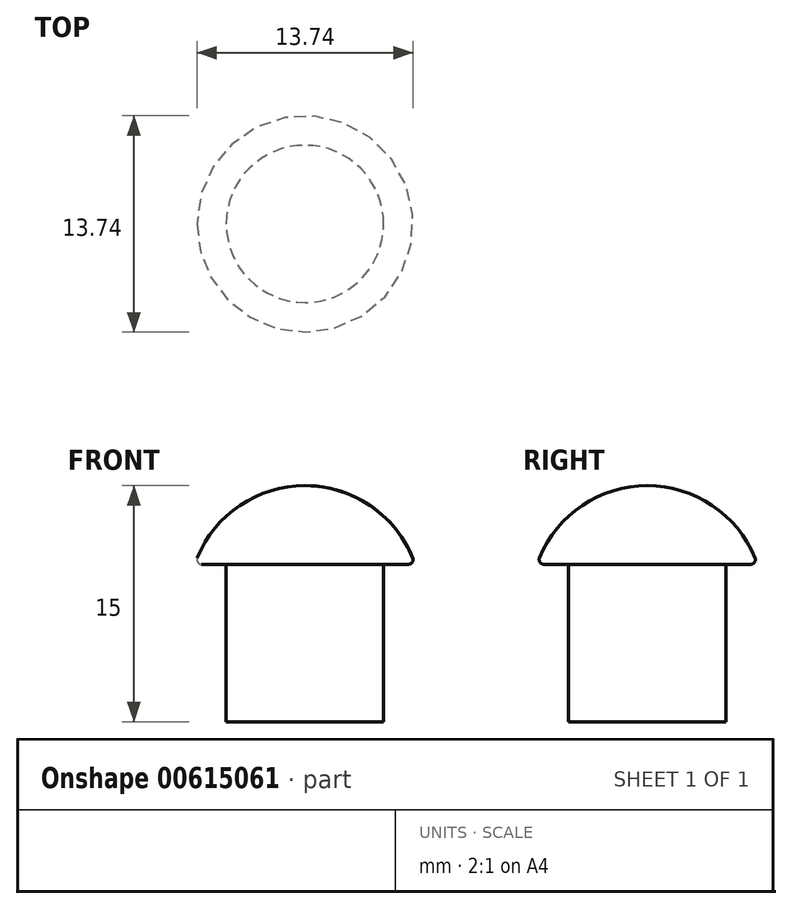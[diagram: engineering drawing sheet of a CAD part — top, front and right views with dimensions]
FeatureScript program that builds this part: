
annotation { "Feature Type Name" : "Feature", "Feature Type Description" : "" }
export const myFeature = defineFeature(function(context is Context, id is Id, definition is map)
    precondition{}
    {
        {
            var Q0;
            Q0=qCreatedBy(makeId("Front.planeOp"),FACE);
            var sketch = newSketch(context, id + "F0", { "sketchPlane" : qUnion([Q0])});
            skLineSegment(sketch, "E0", {"start": v(0, 0) * mm, "end": v(5, 0) * mm});
            skLineSegment(sketch, "E1", {"start": v(5, 0) * mm, "end": v(5, 10) * mm});
            skLineSegment(sketch, "E2", {"start": v(5, 10) * mm, "end": v(7, 10) * mm});
            skArc(sketch, "E3", {"start": v(7, 10) * mm, "mid": v(4.3, 13.62) * mm, "end": v(0, 15) * mm});
            skLineSegment(sketch, "E4", {"start": v(0, 0) * mm, "end": v(0, 19.87) * mm, "construction": true});
            skLineSegment(sketch, "E5", {"start": v(0, 0) * mm, "end": v(0, 15) * mm});
            skSolve(sketch);
        }
        {
            var Q0;
            Q0 = qSketchRegion(id + "F0", true);
            var Q1;
            Q1=sQuery(id+"F0.wireOp",EDGE,"E4");
            revolve(context, id + "F1", {"entities" : qUnion([Q0]), "axis" : qUnion([Q1]), "revolveType" : RevolveType.FULL});
        }
        {
            var Q0;
            Q0=makeQuery(id+"F1.opRevolve","SWEPT_EDGE",EDGE,{"disambiguationData":[OSD([sQuery(id+"F0.wireOp",EDGE,"E2"),sQuery(id+"F0.wireOp",EDGE,"E3")])]});
            fillet(context, id + "F2", {"entities" : qUnion([Q0]), "radius" : 0.3 * mm, "tangentPropagation" : true, "allowEdgeOverflow" : false});
        }
    });
